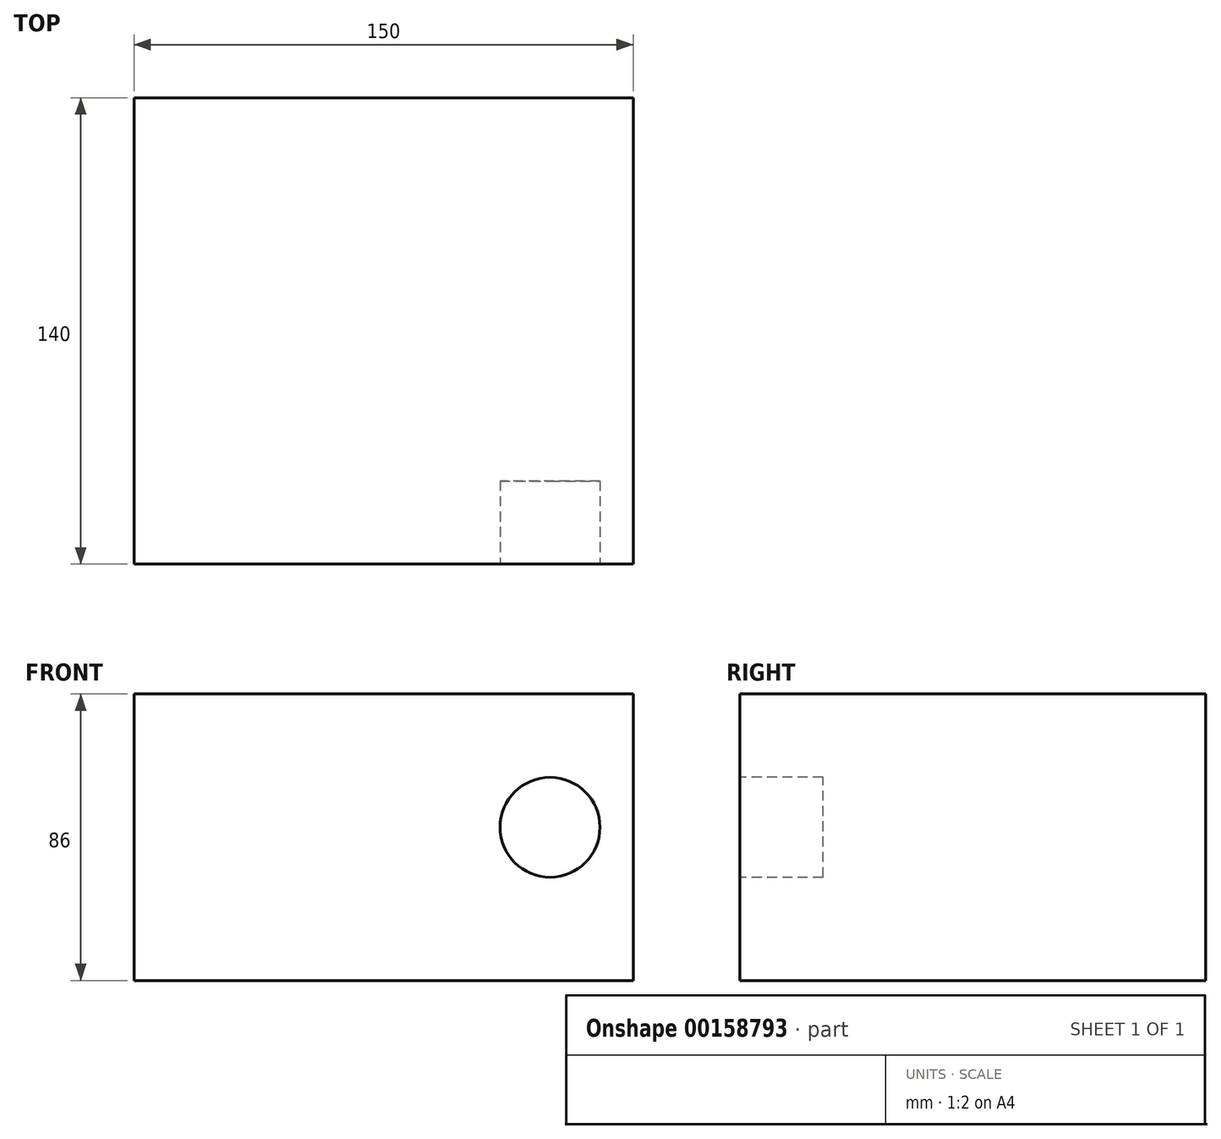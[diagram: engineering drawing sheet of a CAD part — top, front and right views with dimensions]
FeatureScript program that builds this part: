
annotation { "Feature Type Name" : "Feature", "Feature Type Description" : "" }
export const myFeature = defineFeature(function(context is Context, id is Id, definition is map)
    precondition{}
    {
        {
            var Q0;
            Q0=qCreatedBy(makeId("Top.planeOp"),FACE);
            var sketch = newSketch(context, id + "F0", { "sketchPlane" : qUnion([Q0])});
            skLineSegment(sketch, "E0.bottom", {"start": v(75, 70) * mm, "end": v(-75, 70) * mm});
            skLineSegment(sketch, "E0.top", {"start": v(75, -70) * mm, "end": v(-75, -70) * mm});
            skLineSegment(sketch, "E0.left", {"start": v(75, 70) * mm, "end": v(75, -70) * mm});
            skLineSegment(sketch, "E0.right", {"start": v(-75, 70) * mm, "end": v(-75, -70) * mm});
            skPoint(sketch, "E0.middle", {"position": v(0, 0) * mm});
            skSolve(sketch);
        }
        {
            var Q0;
            Q0 = qSketchRegion(id + "F0", true);
            extrude(context, id + "F1", {"entities" : qUnion([Q0]), "depth" : 86 * mm});
        }
        {
            var Q0;
            Q0=makeQuery(id+"F1.opExtrude","SWEPT_FACE",FACE,{"disambiguationData":[OSD([sQuery(id+"F0.wireOp",EDGE,"E0.top")])]});
            var sketch = newSketch(context, id + "F2", { "sketchPlane" : qUnion([Q0])});
            skLineSegment(sketch, "E1.top", {"start": v(75, 46) * mm, "end": v(50, 46) * mm});
            skLineSegment(sketch, "E1.right", {"start": v(50, 86) * mm, "end": v(50, 46) * mm});
            skCircle(sketch, "E2", {"center": v(50, 46) * mm, "radius": 15 * mm});
            skSolve(sketch);
        }
        {
            var Q0;
            Q0 = qSketchRegion(id + "F2", true);
            extrude(context, id + "F3", {"entities" : qUnion([Q0]), "operationType" : NewBodyOperationType.REMOVE, "oppositeDirection" : true, "depth" : 25 * mm});
        }
    });
